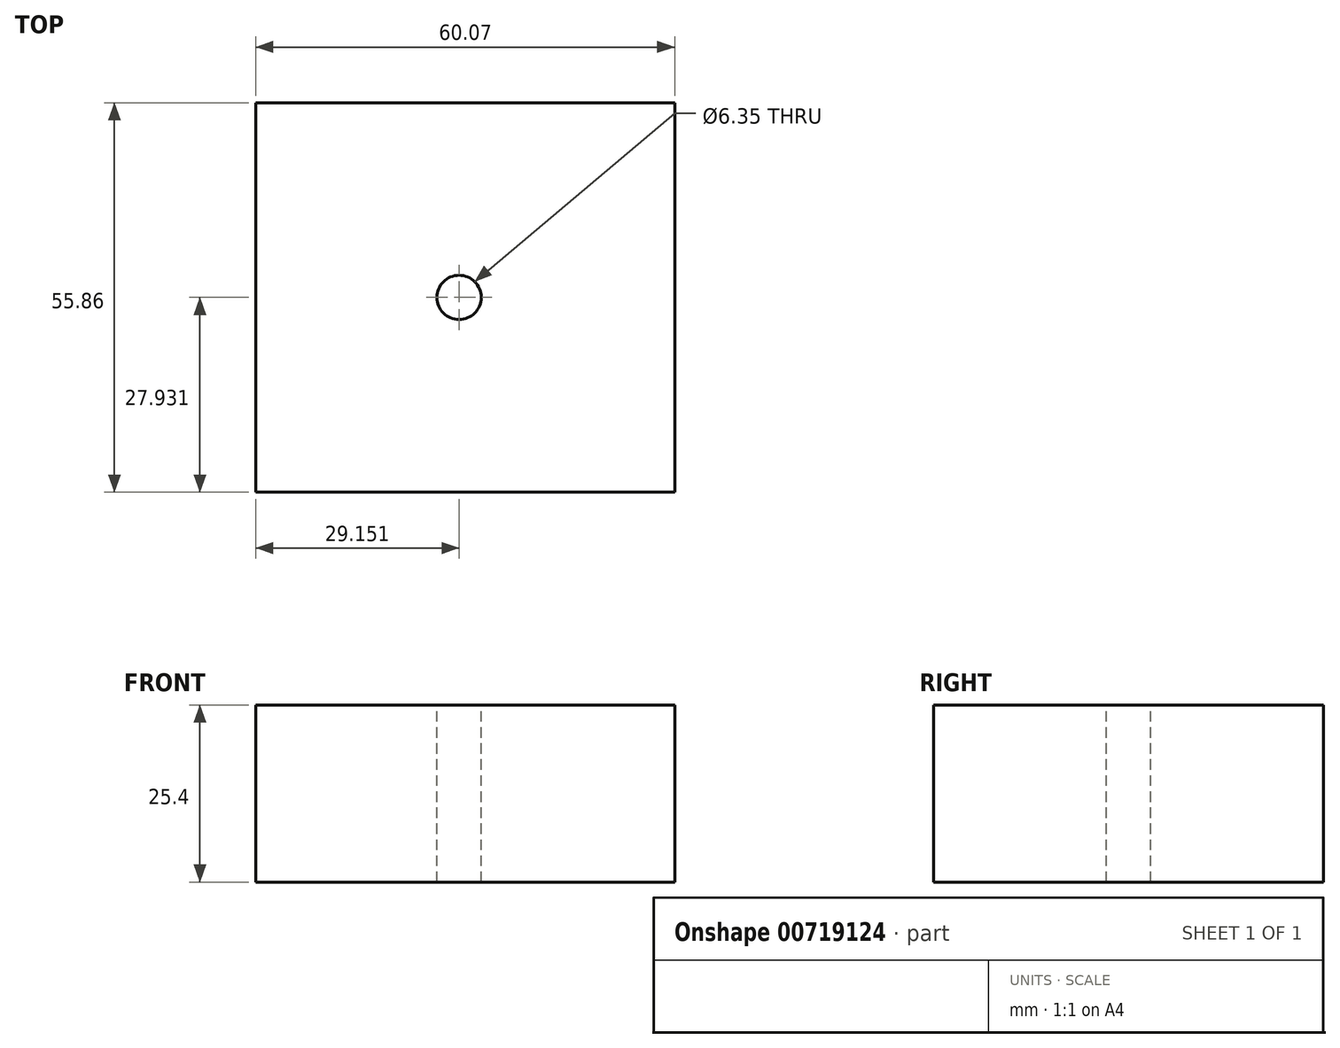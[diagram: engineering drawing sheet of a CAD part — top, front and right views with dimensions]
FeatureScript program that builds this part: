
annotation { "Feature Type Name" : "Feature", "Feature Type Description" : "" }
export const myFeature = defineFeature(function(context is Context, id is Id, definition is map)
    precondition{}
    {
        {
            var Q0;
            Q0=qCreatedBy(makeId("Top.planeOp"),FACE);
            var sketch = newSketch(context, id + "F0", { "sketchPlane" : qUnion([Q0])});
            skLineSegment(sketch, "E0.bottom", {"start": v(0, 0) * mm, "end": v(60.07, 0) * mm});
            skLineSegment(sketch, "E0.top", {"start": v(0, -55.86) * mm, "end": v(60.07, -55.86) * mm});
            skLineSegment(sketch, "E0.left", {"start": v(0, 0) * mm, "end": v(0, -55.86) * mm});
            skLineSegment(sketch, "E0.right", {"start": v(60.07, 0) * mm, "end": v(60.07, -55.86) * mm});
            skSolve(sketch);
        }
        {
            var Q0;
            Q0=makeQuery(id+"F0.imprint","IMPRINT",FACE,{"disambiguationData":[TD([[makeQuery(id+"F0.imprint","IMPRINT",EDGE,{"derivedFrom":sQuery(id+"F0.wireOp",EDGE,"E0.bottom")}),-1.0]])]});
            extrude(context, id + "F1", {"entities" : qUnion([Q0]), "depth" : 25.4 * mm, "offsetDistance" : 25.4 * mm});
        }
        {
            var Q0;
            Q0=makeQuery(id+"F1.opExtrude","CAP_FACE",FACE,{"disambiguationData":[OSD([sQuery(id+"F0.wireOp",EDGE,"E0.bottom"),sQuery(id+"F0.wireOp",EDGE,"E0.top"),sQuery(id+"F0.wireOp",EDGE,"E0.left"),sQuery(id+"F0.wireOp",EDGE,"E0.right")])],"isStart":false});
            var sketch = newSketch(context, id + "F2", { "sketchPlane" : qUnion([Q0])});
            skPoint(sketch, "E1", {"position": v(29.15, -27.93) * mm});
            skPoint(sketch, "E1.positionSnap0", {"position": v(0, -27.93) * mm});
            skSolve(sketch);
        }
        {
            var Q0;
            Q0=sQuery(id+"F2.wireOp",VERTEX,"E1");
            var Q1;
            Q1=makeQuery(id+"F1.opExtrude","SWEPT_BODY",BODY,{"disambiguationData":[OSD([sQuery(id+"F0.wireOp",EDGE,"E0.bottom"),sQuery(id+"F0.wireOp",EDGE,"E0.top"),sQuery(id+"F0.wireOp",EDGE,"E0.left"),sQuery(id+"F0.wireOp",EDGE,"E0.right")])]});
            hole(context, id + "F3", {"style" : HoleStyle.SIMPLE, "endStyle" : HoleEndStyle.THROUGH, "holeDiameter" : 6.35 * mm, "majorDiameter" : 6.35 * mm, "isTappedThrough" : true, "tappedDepth" : 12.7 * mm, "tapClearance" : 3, "locations" : qUnion([Q0]), "scope" : qUnion([Q1])});
        }
    });
